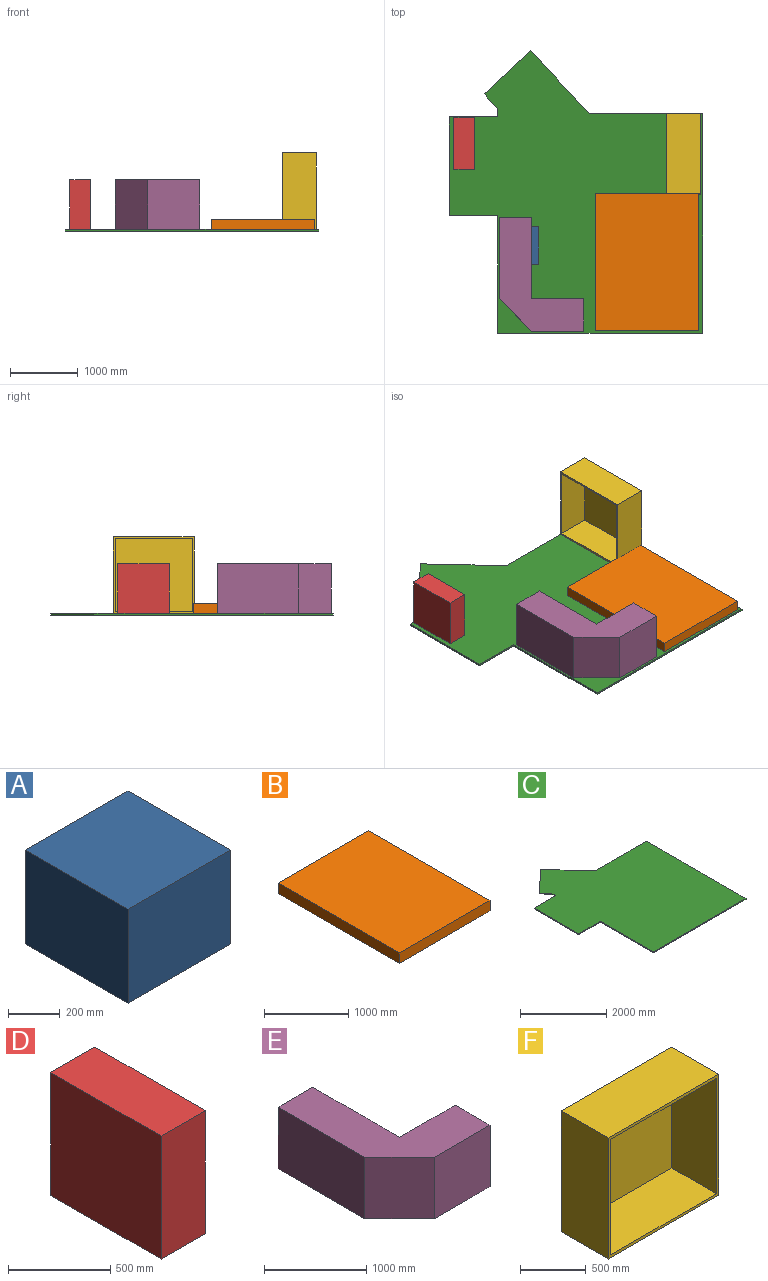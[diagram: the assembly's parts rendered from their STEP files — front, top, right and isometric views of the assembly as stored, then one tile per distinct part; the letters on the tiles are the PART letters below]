
ASSEMBLY  parts=6 mates=5
PART A: 6 faces, bbox 558.8x558.8x444.5 mm
  f0: plane 558.8x444.5mm, normal (-1,0,0), area 248386.6mm2, adj f1,f3,f4,f5
  f1: plane 558.8x444.5mm, normal (0,-1,0), area 248386.6mm2, adj f0,f2,f4,f5
  f2: plane 558.8x444.5mm, normal (1,0,0), area 248386.6mm2, adj f1,f3,f4,f5
  f3: plane 558.8x444.5mm, normal (0,1,0), area 248386.6mm2, adj f0,f2,f4,f5
  f4: plane 558.8x558.8mm, normal (0,0,1), area 312257.4mm2, adj f0,f1,f2,f3
  f5: plane 558.8x558.8mm, normal (0,0,-1), area 312257.4mm2, adj f0,f1,f2,f3
PART B: 6 faces, bbox 1524x2032x152.4 mm
  f0: plane 1524x152.4mm, normal (0,-1,0), area 232257.6mm2, adj f1,f3,f4,f5
  f1: plane 2032x152.4mm, normal (1,0,0), area 309676.8mm2, adj f0,f2,f4,f5
  f2: plane 1524x152.4mm, normal (0,1,0), area 232257.6mm2, adj f1,f3,f4,f5
  f3: plane 2032x152.4mm, normal (-1,0,0), area 309676.8mm2, adj f0,f2,f4,f5
  f4: plane 2032x1524mm, normal (0,0,1), area 3096768mm2, adj f0,f1,f2,f3
  f5: plane 2032x1524mm, normal (0,0,-1), area 3096768mm2, adj f0,f1,f2,f3
PART C: 13 faces, bbox 3741.7x4181.3x25.4 mm
  f0: plane 1739.9x25.4mm, normal (-1,0,0), area 44193.5mm2, adj f1,f10,f11,f12
  f1: plane 3030.54x25.4mm, normal (0,-1,0), area 76975.8mm2, adj f0,f2,f11,f12
  f2: plane 3251.2x25.4mm, normal (1,0,0), area 82580.5mm2, adj f1,f3,f11,f12
  f3: plane 1676.4x25.4mm, normal (0,1,0), area 42580.6mm2, adj f2,f4,f11,f12
  f4: plane 930.07x864.8mm, normal (0.73,0.68,0), area 32258mm2, adj f3,f5,f11,f12
  f5: plane 688.25x639.95mm, normal (-0.68,0.73,0), area 23870.9mm2, adj f4,f6,f11,f12
  f6: plane 213.92x198.9mm, normal (-0.73,-0.68,0), area 7419.3mm2, adj f5,f7,f11,f12
  f7: plane 127x25.4mm, normal (-1,0,0), area 3225.8mm2, adj f6,f8,f11,f12
  f8: plane 711.2x25.4mm, normal (0,1,0), area 18064.5mm2, adj f7,f9,f11,f12
  f9: plane 1460.5x25.4mm, normal (-1,0,0), area 37096.7mm2, adj f8,f10,f11,f12
  f10: plane 711.2x25.4mm, normal (0,-1,0), area 18064.5mm2, adj f0,f9,f11,f12
  f11: plane 4181.27x3741.74mm, normal (0,0,-1), area 11677236mm2, adj f0,f1,f2,f3,f4,f5,f6,f7
  f12: plane 4181.27x3741.74mm, normal (0,0,1), area 11677236mm2, adj f0,f1,f2,f3,f4,f5,f6,f7
PART D: 11 faces, bbox 304.8x762x736.6 mm
  f0: plane 762x736.6mm, normal (1,0,0), area 73548.2mm2, adj f1,f3,f4,f5,f6,f8,f9,f10
  f1: plane 736.6x304.8mm, normal (0,1,0), area 224515.7mm2, adj f0,f2,f4,f5
  f2: plane 762x736.6mm, normal (-1,0,0), area 561289.2mm2, adj f1,f3,f4,f5
  f3: plane 736.6x304.8mm, normal (0,-1,0), area 224515.7mm2, adj f0,f2,f4,f5
  f4: plane 762x304.8mm, normal (0,0,1), area 232257.6mm2, adj f0,f1,f2,f3
  f5: plane 762x304.8mm, normal (0,0,-1), area 232257.6mm2, adj f0,f1,f2,f3
  f6: plane 685.8x279.4mm, normal (0,-1,0), area 191612.5mm2, adj f0,f7,f9,f10
  f7: plane 711.2x685.8mm, normal (1,0,0), area 487741mm2, adj f6,f8,f9,f10
  f8: plane 685.8x279.4mm, normal (0,1,0), area 191612.5mm2, adj f0,f7,f9,f10
  f9: plane 711.2x279.4mm, normal (0,0,-1), area 198709.3mm2, adj f0,f6,f7,f8
  f10: plane 711.2x279.4mm, normal (0,0,1), area 198709.3mm2, adj f0,f6,f7,f8
PART E: 16 faces, bbox 1249.9x1680x735.1 mm
  f0: plane 735.08x480.06mm, normal (0,1,0), area 41767.7mm2, adj f1,f4,f8,f9,f10,f11,f14,f15
  f1: plane 1199.9x25.4mm, normal (1,0,0), area 30477.4mm2, adj f0,f2,f10,f15
  f2: plane 769.87x25.4mm, normal (0,1,0), area 19554.8mm2, adj f1,f3,f10,f15
  f3: plane 735.08x480.06mm, normal (1,0,0), area 41767.7mm2, adj f2,f6,f7,f9,f10,f13,f14,f15
  f4: plane 1199.9x735.08mm, normal (-1,0,0), area 882014.8mm2, adj f0,f5,f9,f10
  f5: plane 735.08x480.06mm, normal (-0.71,-0.71,0), area 499048.5mm2, adj f4,f6,f9,f10
  f6: plane 769.87x735.08mm, normal (0,-1,0), area 565915.9mm2, adj f3,f5,f9,f10
  f7: plane 769.87x25.4mm, normal (0,1,0), area 19554.8mm2, adj f3,f8,f9,f14
  f8: plane 1199.9x25.4mm, normal (1,0,0), area 30477.4mm2, adj f0,f7,f9,f14
  f9: plane 1679.96x1249.93mm, normal (0,0,1), area 1060836.6mm2, adj f0,f3,f4,f5,f6,f7,f8
  f10: plane 1679.96x1249.93mm, normal (0,0,-1), area 1060836.6mm2, adj f0,f1,f2,f3,f4,f5,f6
  f11: plane 1189.38x684.28mm, normal (1,0,0), area 813860.8mm2, adj f0,f12,f14,f15
  f12: plane 684.28x465.18mm, normal (0.71,0.71,0), area 450161.4mm2, adj f11,f13,f14,f15
  f13: plane 759.35x684.28mm, normal (0,1,0), area 519607mm2, adj f3,f12,f14,f15
  f14: plane 1654.56x1224.53mm, normal (0,0,-1), area 994094.7mm2, adj f0,f3,f7,f8,f11,f12,f13
  f15: plane 1654.56x1224.53mm, normal (0,0,1), area 994094.7mm2, adj f0,f1,f2,f3,f11,f12,f13
PART F: 11 faces, bbox 1193.8x508x1130.3 mm
  f0: plane 1193.8x1130.3mm, normal (0,-1,0), area 115483.6mm2, adj f2,f3,f4,f5,f7,f8,f9,f10
  f1: plane 1193.8x1130.3mm, normal (0,1,0), area 1349352.1mm2, adj f2,f3,f4,f5
  f2: plane 1130.3x508mm, normal (-1,0,0), area 574192.4mm2, adj f0,f1,f4,f5
  f3: plane 1130.3x508mm, normal (1,0,0), area 574192.4mm2, adj f0,f1,f4,f5
  f4: plane 1193.8x508mm, normal (0,0,1), area 606450.4mm2, adj f0,f1,f2,f3
  f5: plane 1193.8x508mm, normal (0,0,-1), area 606450.4mm2, adj f0,f1,f2,f3
  f6: plane 1143x1079.5mm, normal (0,-1,0), area 1233868.5mm2, adj f7,f8,f9,f10
  f7: plane 1079.5x482.6mm, normal (1,0,0), area 520966.7mm2, adj f0,f6,f9,f10
  f8: plane 1079.5x482.6mm, normal (-1,0,0), area 520966.7mm2, adj f0,f6,f9,f10
  f9: plane 1143x482.6mm, normal (0,0,-1), area 551611.8mm2, adj f0,f6,f7,f8
  f10: plane 1143x482.6mm, normal (0,0,1), area 551611.8mm2, adj f0,f6,f7,f8
PLACE A t=(52.18,1019.88,0)mm
PLACE B t=(1450.47,39.68,0)mm
PLACE C at identity fixed
PLACE D t=(-646.35,2425.9,0)mm
PLACE E t=(25.81,511.87,0)mm
PLACE F rot(axis=(0,0,-1),90deg) t=(2490.42,3253.27,0)mm
MATE planar C.f12 <-> A.f5  axis (0,0,1) through (1281.45,1832.43,0)mm
MATE planar B.f5 <-> C.f12  axis (0,0,-1) through (2212.47,39.68,0)mm
MATE planar D.f5 <-> C.f12  axis (0,0,-1) through (-493.95,2806.9,0)mm
MATE planar E.f10 <-> C.f12  axis (0,0,-1) through (505.87,1711.77,0)mm
MATE planar F.f5 <-> C.f12  axis (0,0,-1) through (2744.42,2059.47,0)mm
